# Revit family: Solido Smart cistilna naprava - PVC_Light
name_source: partatom
category: Specialty Equipment
revit_build: Autodesk Revit Architecture 2015 (Build: 20140606_1530(x64)
units: mm (PartAtom-declared; Revit-internal decimal feet)

## types (2) — shared parameters
Description = Biološka čistilna naprava Solido SMART z plastičnim rezervoarjem.
GZS list of Water Treatement Plant = https://www.gzs.si
Instalation Instructions = http://www.gorec.info
Length = 2420 mm  [stored 7.93963 ft]
Manufacturer = Gorec
Manufacturer Website = http://www.gorec.info
Material = <By Category>
Model = KCBL4500 Solido SMART C
Note = Vtočna cev fi110, fi125, fi160.
Pipe Diameter = 110 mm  [stored 0.360892 ft]
Product Certification = SIST EN 12566-3
Pump Type = Kompresorska zračna črpalka
URL = http://www.gorec.info
Voltage = 220 $
You Tube = https://www.youtube.com
zero-valued in all types: Default Elevation

## per-type parameters (varying)
| type | Diameter | Height | Max. Daily Water Flow (l) | Size | Volume | Weight |
| 2 do 5 PE | 1420 mm  [stored 4.65879 ft] | 2090 mm  [stored 6.85696 ft] | 900 | 3000L | 3000 m³ | 150.00 kg |
| 6 do 8 PE | 1700 mm  [stored 5.57743 ft] | 2370 mm  [stored 7.77559 ft] | 1350 | 4500L | 4500 m³ | 200.00 kg |

note: [stored X ft] marks values corroborated as IEEE doubles in the binary element streams (Revit-internal decimal feet)

## geometry (parser evidence)
native form markers: Blend x24, Sweep x48
no freeform markers — native parametric forms only
